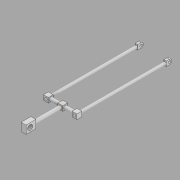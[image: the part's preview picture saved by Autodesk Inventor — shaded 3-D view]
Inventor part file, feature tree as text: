
AUTODESK INVENTOR PART (.ipt)
format: ipt  version: 2020 (Build 240168000, 168)  size: 180,736 bytes
history: native  units: in
note: dims shown in document units (in); Inventor stores cm internally (conversion verified against a paired STEP export)
features: extrude x9, sketch x9, plane x2, other x1, projected_geometry x1
ambient origin geometry x8: Origin, YZ Plane, XZ Plane, XY Plane, X Axis, Y Axis, Z Axis, Center Point
bodies: Body1 (feature_tree)
feature tree (22):
  other  "Sólido1"
  extrude  "Extrusión1"  Depth=0.1875in
  extrude  "Extrusión2"  Depth=0.1875in TaperAngle=0.0deg
  extrude  "Extrusión3"  Depth=0.3594in TaperAngle=0.0deg
  extrude  "Extrusión4"  Depth=0.3594in TaperAngle=0.0deg
  extrude  "Extrusión5"  Depth=0.1875in
  extrude  "Extrusión6"  Depth=0.1875in
  extrude  "Extrusión7"  Depth=0.5469in
  plane  "Plano de trabajo1"
  extrude  "Extrusión8"  Depth=0.0938in
  plane  "Plano de trabajo2"
  extrude  "Extrusión9"  Depth=1.0313in TaperAngle=0.0deg
  sketch  "Boceto1"  dims[d0=0.1875in d1=0.1875in]
  sketch  "Boceto2"  dims[d2=0.125in d3=0.1875in d4=0.0in]
  sketch  "Boceto3"  dims[d5=0.125in d6=0.3594in d7=0.0in]
  sketch  "Boceto4"  dims[d8=0.125in d9=0.3594in d10=0.0in]
  sketch  "Boceto5"  dims[d11=0.1875in d12=0.1875in]
  sketch  "Boceto6"  dims[d13=0.1875in d14=0.1875in]
  sketch  "Boceto7"  dims[d15=0.5469in d16=0.5469in]
  sketch  "Boceto8"  dims[d17=0.0938in d18=0.0938in]
  sketch  "Boceto9"  dims[d19=0.1875in d20=0.0in d21=1.0313in d22=0.0in d23=0.3125in d24=0.375in d25=1.2188in d26=0.1875in d27=0.1562in d28=0.1875in d29=0.0in d30=3.2812in d31=0.0in d32=0.5469in d33=0.1875in d34=3.5in d35=0.0938in d36=0.0938in d37=0.0in d38=-0.5469in d39=0.0938in d40=0.0in]
  projected_geometry  "Contorno proyectado1"
